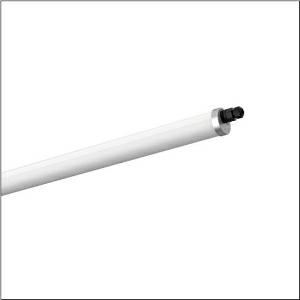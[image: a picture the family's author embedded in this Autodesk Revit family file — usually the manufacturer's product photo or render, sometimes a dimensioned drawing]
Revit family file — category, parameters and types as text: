
# Revit family: monsun_31_tube_51ft10dn480a
name_source: partatom
category: Lighting Fixtures
units: mm (PartAtom-declared; Revit-internal decimal feet)

## family parameters
Cut with Voids When Loaded = No
Host = Face
Light Source = No
Part Type = Normal
Room Calculation Point = No
Round Connector Dimension = Use Diameter
Shared = No

## types (1)
- Monsun 31 Tube (1 x LED, 8000 lm, 50 W, 4000K)
    Apparent Load = 50 VA
    CIE Flux Codes = 42 71 89 91 100
    Color Rendering = 80
    Color Temperature = 4000K
    Default Elevation = 1800 mm
    Description = Monsun 31 Tube, tubular luminaire, primary optical cover: diffuser, of PMMA, light emission: direct distribution, primary light characteristic: symmetric, installation type: suspended mounting, surface-mounted, LED, rated luminous flux: 8.000lm, luminous efficacy: 160lm/W, light colour: 840, colour temperature: 4000K, control gear: DALI 2, with with 1 terminal, 5-pole, max. 2.5mm², through-wiring: 5x 1.5mm², mains connection: 220..240V, AC, 50/60Hz, rated input power: 50W, housing, cylindrical, of PMMA, semi-transparent, matt white, with luminaire and ceiling fastening, V4A, mounting with brackets of stainless steel, length: 1.570mm, diameter: 75mm, end cap, of stainless steel (V4A), protection rating (complete): IP67/IP69K, insulation class (complete): insulation class I (protective earthing), certification: CE, UKCA, impact resistance: IK07, permissible operating ambient temperature: -20..+40°C, corresponds to IFS (International Featured Standards) requirements for safety and quality in the food industry, usage in unprotected outdoor areas possible with horizontal mounting, contact your sales advisor before using the luminaires in applications with unclear chemical exposure, large temperature fluctuations or condensation-forming humidity, packaging unit: 1 piece
    Height = 83 mm
    Lamp = 1 x LED
    Lamp Light Flux = 8000 lm
    Lamp Power = 50 W
    Lamp count = 1
    Length = 1570 mm
    Luminous efficacy = 160 lm/W
    Manufacturer = Siteco
    ModVariant = No
    Model = 51FT10DN480A
    Mounting Place = Ceiling
    Mounting Type = Pendant
    Number of Poles = 1
    OnlyDefault = Yes
    Power Factor = 1
    Product Name = Monsun 31 Tube
    Product group = tubular luminaire
    ProductGroupID = 906
    Protection Class = Protection class I
    RLX_Detail_Level = 1
    RLX_Emergency_Light_Flux = 0 lm
    RLX_Emergency_Type = 0
    RLX_Emergency_Type_DB = No
    RlxData = <blob elided: 25317 chars, md5=7a960642>
    Socket = socket
    Standby Power = 0 W
    System Light Flux = 8000 lm
    System Power = 50 W
    Type Comments = Product without accessories
    Type Image = l_1228461.jpg
    URL = http://relux.com
    VarID = ---
    Voltage = 0 V
    Weight = 0.00 kg
    Width = 75 mm

## geometry (parser evidence)
native form markers: Blend x4, Sweep x15
no freeform markers — native parametric forms only
